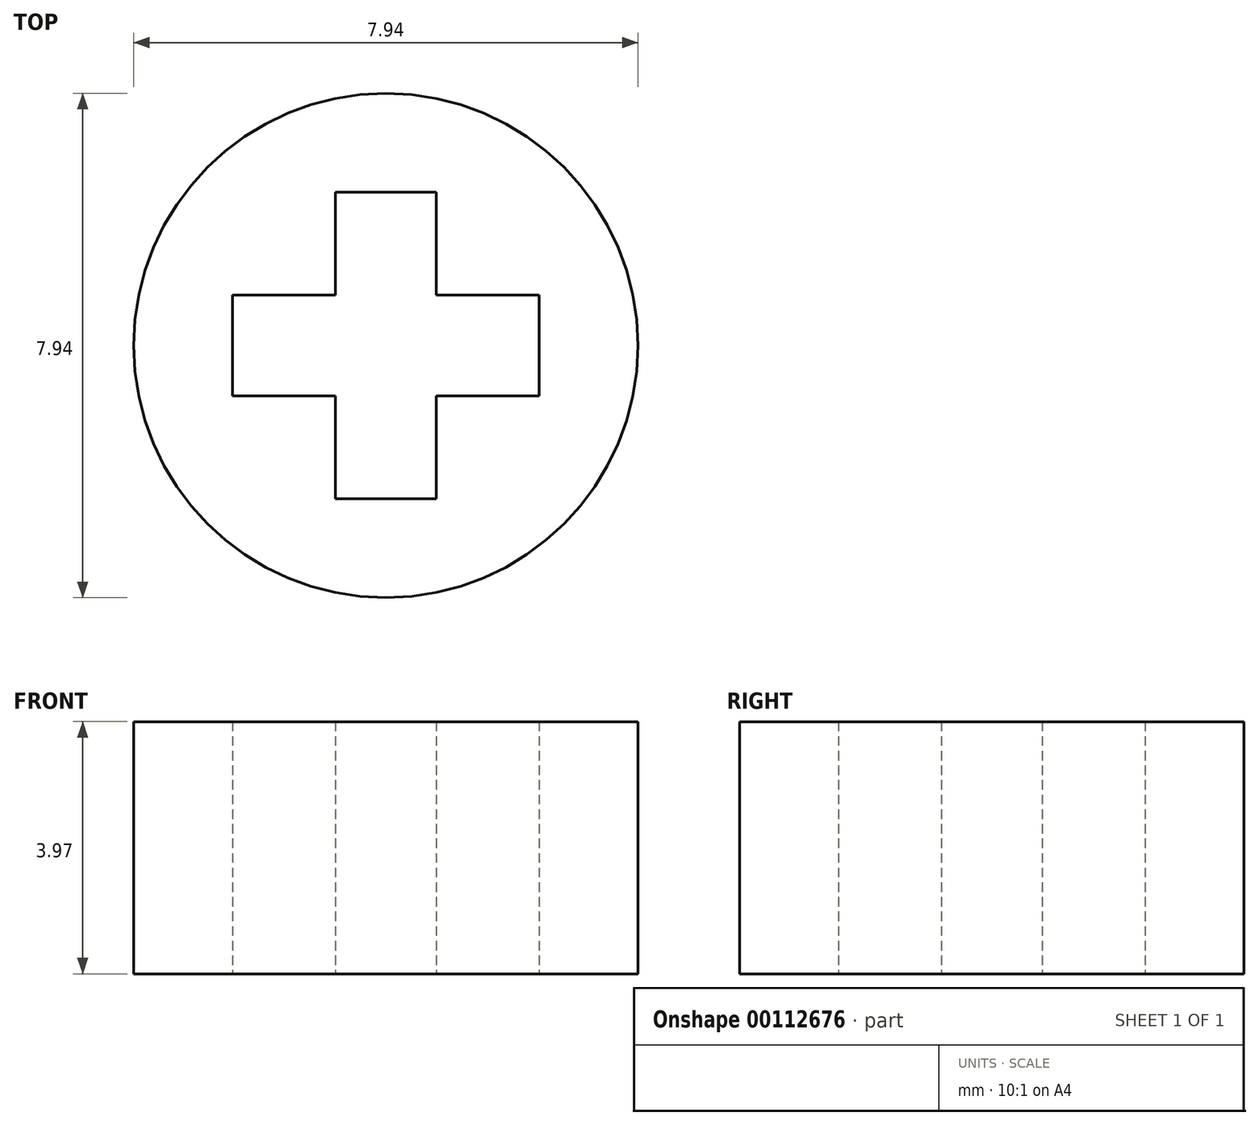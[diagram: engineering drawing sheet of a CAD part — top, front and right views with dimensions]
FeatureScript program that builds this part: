
annotation { "Feature Type Name" : "Feature", "Feature Type Description" : "" }
export const myFeature = defineFeature(function(context is Context, id is Id, definition is map)
    precondition{}
    {
        {
            var Q0;
            Q0=qCreatedBy(makeId("Top.planeOp"),FACE);
            var sketch = newSketch(context, id + "F0", { "sketchPlane" : qUnion([Q0])});
            skCircle(sketch, "E0", {"center": v(0, 0) * mm, "radius": 3.97 * mm});
            skLineSegment(sketch, "E1.bottom", {"start": v(0.8, -2.41) * mm, "end": v(-0.8, -2.41) * mm});
            skLineSegment(sketch, "E1.top", {"start": v(0.8, 2.41) * mm, "end": v(-0.8, 2.41) * mm});
            skLineSegment(sketch, "E1.left", {"start": v(0.8, -2.41) * mm, "end": v(0.8, 2.41) * mm});
            skLineSegment(sketch, "E1.right", {"start": v(-0.8, -2.41) * mm, "end": v(-0.8, 2.41) * mm});
            skLineSegment(sketch, "E2.bottom", {"start": v(2.41, -0.8) * mm, "end": v(-2.41, -0.8) * mm});
            skLineSegment(sketch, "E2.top", {"start": v(2.41, 0.8) * mm, "end": v(-2.41, 0.8) * mm});
            skLineSegment(sketch, "E2.left", {"start": v(2.41, -0.8) * mm, "end": v(2.41, 0.8) * mm});
            skLineSegment(sketch, "E2.right", {"start": v(-2.41, -0.8) * mm, "end": v(-2.41, 0.8) * mm});
            skSolve(sketch);
        }
        {
            var Q0;
            Q0 = qSketchRegion(id + "F0", true);
            extrude(context, id + "F1", {"entities" : qUnion([Q0]), "depth" : 3.97 * mm});
        }
    });
